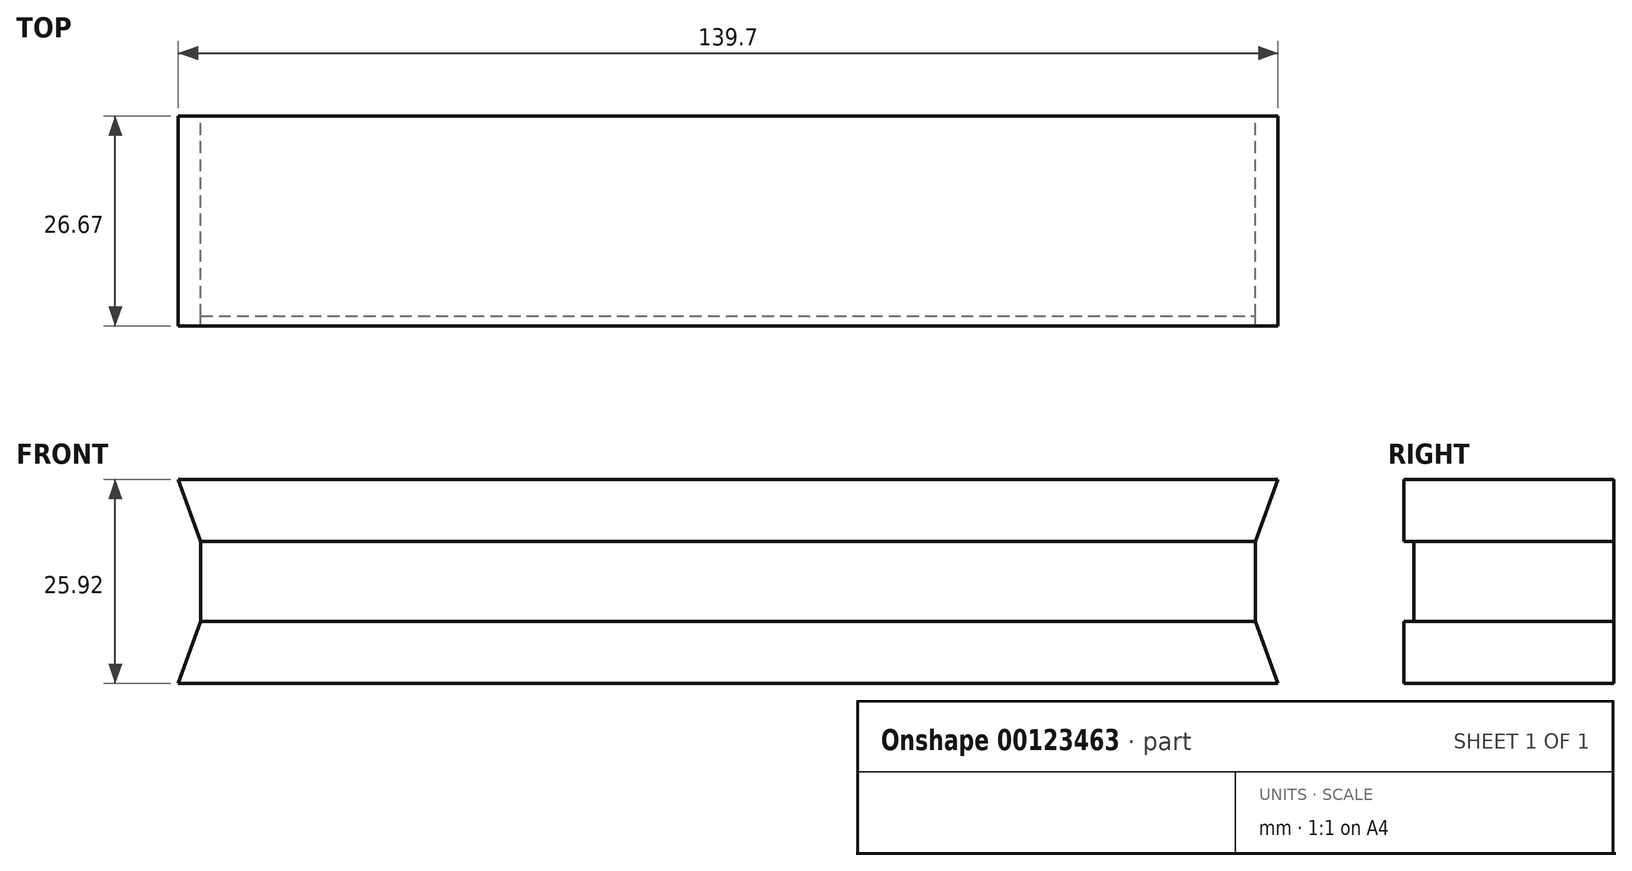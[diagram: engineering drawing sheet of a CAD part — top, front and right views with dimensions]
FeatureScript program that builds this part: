
annotation { "Feature Type Name" : "Feature", "Feature Type Description" : "" }
export const myFeature = defineFeature(function(context is Context, id is Id, definition is map)
    precondition{}
    {
        {
            var Q0;
            Q0=qCreatedBy(makeId("Front.planeOp"),FACE);
            var sketch = newSketch(context, id + "F0", { "sketchPlane" : qUnion([Q0])});
            skLineSegment(sketch, "E0", {"start": v(-73.42, 16.63) * mm, "end": v(66.28, 16.63) * mm});
            skLineSegment(sketch, "E1", {"start": v(66.28, -9.29) * mm, "end": v(-73.42, -9.29) * mm});
            skLineSegment(sketch, "E2", {"start": v(66.28, 16.63) * mm, "end": v(63.41, 8.75) * mm});
            skLineSegment(sketch, "E3", {"start": v(63.41, 8.75) * mm, "end": v(63.41, -1.4) * mm});
            skLineSegment(sketch, "E4", {"start": v(63.41, -1.4) * mm, "end": v(66.28, -9.29) * mm});
            skLineSegment(sketch, "E5", {"start": v(-73.42, 16.63) * mm, "end": v(-70.55, 8.75) * mm});
            skLineSegment(sketch, "E6", {"start": v(-70.55, 8.75) * mm, "end": v(-70.55, -1.4) * mm});
            skLineSegment(sketch, "E7", {"start": v(-70.55, -1.4) * mm, "end": v(-73.42, -9.29) * mm});
            skSolve(sketch);
        }
        {
            var Q0;
            Q0=makeQuery(id+"F0.imprint","IMPRINT",FACE,{"disambiguationData":[TD([[makeQuery(id+"F0.imprint","IMPRINT",EDGE,{"derivedFrom":sQuery(id+"F0.wireOp",EDGE,"E0")}),-1.0]])]});
            extrude(context, id + "F1", {"entities" : qUnion([Q0]), "depth" : 25.4 * mm});
        }
        {
            var Q0;
            Q0=makeQuery(id+"F1.opExtrude","CAP_FACE",FACE,{"disambiguationData":[OSD([sQuery(id+"F0.wireOp",EDGE,"E0"),sQuery(id+"F0.wireOp",EDGE,"E1"),sQuery(id+"F0.wireOp",EDGE,"E2"),sQuery(id+"F0.wireOp",EDGE,"E3"),sQuery(id+"F0.wireOp",EDGE,"E4"),sQuery(id+"F0.wireOp",EDGE,"E5"),sQuery(id+"F0.wireOp",EDGE,"E6"),sQuery(id+"F0.wireOp",EDGE,"E7")])],"isStart":false});
            var sketch = newSketch(context, id + "F2", { "sketchPlane" : qUnion([Q0])});
            skLineSegment(sketch, "E8", {"start": v(-70.55, 8.75) * mm, "end": v(63.41, 8.75) * mm});
            skLineSegment(sketch, "E9", {"start": v(-70.55, -1.4) * mm, "end": v(63.41, -1.4) * mm});
            skSolve(sketch);
        }
        {
            var Q0;
            Q0=makeQuery(id+"F2.imprint","IMPRINT",FACE,{"disambiguationData":[TD([[makeQuery(id+"F2.imprint","IMPRINT",EDGE,{"derivedFrom":sQuery(id+"F2.wireOp",EDGE,"E8")}),1.0]])]});
            extrude(context, id + "F3", {"entities" : qUnion([Q0]), "operationType" : NewBodyOperationType.ADD, "depth" : 1.27 * mm});
        }
        {
            var Q0;
            Q0=makeQuery(id+"F2.imprint","IMPRINT",FACE,{"disambiguationData":[TD([[makeQuery(id+"F2.imprint","IMPRINT",EDGE,{"derivedFrom":sQuery(id+"F2.wireOp",EDGE,"E9")}),-1.0]])]});
            extrude(context, id + "F4", {"entities" : qUnion([Q0]), "operationType" : NewBodyOperationType.ADD, "depth" : 1.27 * mm});
        }
    });
